# Revit family: LDA_BIM_MICROFONO MULTIZONA_MPS-8Z
name_source: partatom
category: Equipos especializados
units: mm (PartAtom-declared; Revit-internal decimal feet)

## family parameters
Compartido = No
Corte con vacíos al cargar = Sí
Cota de conector redondo = Diámetro de uso
Número OmniClass = 23.85.05.17
Punto de cálculo de habitación = No
Se basa en plano de trabajo = Sí
Siempre vertical = No
Tipo de pieza = Normal
Título OmniClass = Complete Audio-Visual Systems

## types (1)
- MPS-8Z
    ACSI Bus = 2 x Audio Balanceado (In+Loop)1Vp, 0,707Vrms. 10 KΩ, 2 x RJ-45 Female, Total 800m. / 2624,7ft
    Acabado = Fe, Gris RAL 7016
    Aux Mic Entrada = 1 x de entrada no Balanceada, 15mV, 47 KΩ, 1 x Minijack Mono 2,5mm
    Axis Direccional = Axial con respuesta diagrama hipercardioid polar.
    Botones = 3 x funciones programables, 1 x recall, 1 x seleccionar/ des-seleccionar todas las zonas, 8 x selección de zonas, 1 x llamar.
    Condiciones de Operación = -5 ºC to +45 ºC / 23 ºF to 113 ºF 5% to 95% Humedad relativa (sin condensación)
    Consumo de energía = 1 A
    Descripción = Micrófono multizona de altas prestaciones para el sistema de evacuación por voz y megafonía de NEO.
    Dimensiones sin gooseneck (W x H x D) = 95 x 65 x 190 mm / 3,75”x 2,56”x 7,48”
    Elevación por defecto = 0 mm  [stored 0 ft]
    Fabricante = LDA
    Fuente de alimentación = 5V dc, Tipo A/B Conector MiniUSB
    Imagen de tipo = <Ninguno>
    Indicadores = Estado: Emergencia, Fallo, Link, Ocupado, Linea Ocupada, Palabra concedida. 8 indicadores de zona seleccionada. Gooseneck incluye anillo luminoso para la palabra concedida
    Longitud Gooseneck = 350mm / 13,78”
    Modelo = MPS-8Z
    Peso = 0,93 kg
    Ratio señal/ruido = R> 98dB, A-ponderado
    Referencia = LDAMPS8ZS02
    Respuesta en frecuencia = 200- 15000 Hz (+/-2dB).
    Sensibilidad = -43 dB. a 1KHz
    Tipo de TransductorConexión = Condensador
    URL = https://support.lda-audiotech.com

note: [stored X ft] marks values corroborated as IEEE doubles in the binary element streams (Revit-internal decimal feet)
